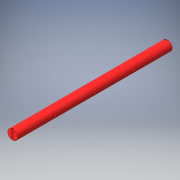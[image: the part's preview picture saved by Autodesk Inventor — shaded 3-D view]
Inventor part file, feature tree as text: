
AUTODESK INVENTOR PART (.ipt)
format: ipt  version: 2016 (Build 200138000, 138)  size: 137,728 bytes
history: native  units: in
note: dims shown in document units (in); Inventor stores cm internally (conversion verified against a paired STEP export)
features: extrude x4, sketch x3
ambient origin geometry x8: Origin, YZ Plane, XZ Plane, XY Plane, X Axis, Y Axis, Z Axis, Center Point
bodies: Solid1 (feature_tree)
feature tree (7):
  extrude  "Extrusion1"  Depth=8.0in TaperAngle=0.0deg
  extrude  "Extrusion4"  Depth=0.06in
  extrude  "Extrusion6"  Depth=2.0in TaperAngle=0.0deg
  extrude  "Extrusion8"  Depth=2.0in
  sketch  "Sketch1"  dims[d0=0.5in d1=8.0in d2=0.0in]
  sketch  "Sketch4"  dims[d13=0.06in d15=0.06in]
  sketch  "Sketch7"  dims[d16=0.1in d17=0.6in d18=0.0in d19=0.1in d20=0.06in d21=0.05in d26=0.5in d27=0.06in d28=1.0in d29=0.0in d42=2.0in d43=0.1in d44=2.0in d45=0.1in d46=2.0in d47=0.1in d48=1.0in d49=0.0in]
